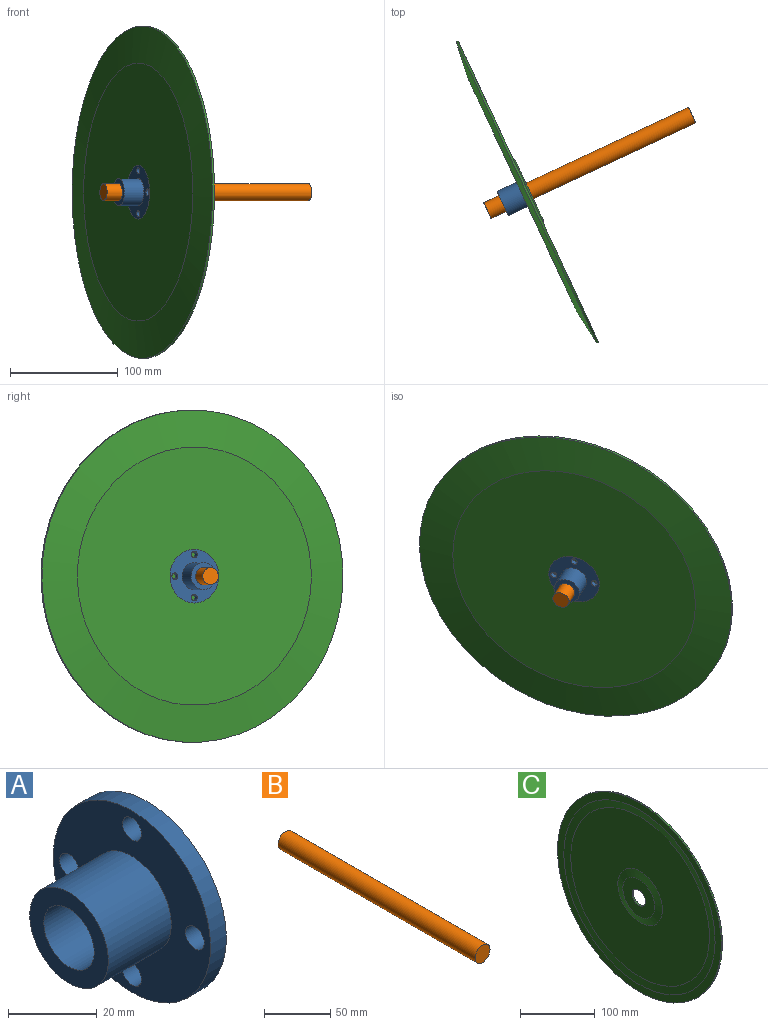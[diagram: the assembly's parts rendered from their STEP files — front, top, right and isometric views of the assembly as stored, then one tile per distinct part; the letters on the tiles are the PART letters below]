
ASSEMBLY  parts=3 mates=2
PART A: 10 faces, bbox 25x50x50 mm
  f0: plane 50x50mm, normal (1,0,0), area 1649.3mm2, adj f1,f5,f6,f7,f8,f9
  f1: cylinder r=25mm len=50mm, axis (1,0,0), area 785.4mm2, adj f0,f2
  f2: plane 50x50mm, normal (-1,0,0), area 1359.5mm2, adj f1,f3,f6,f7,f8,f9
  f3: cylinder r=12.5mm len=25mm, axis (1,0,0), area 1570.8mm2, adj f2,f4
  f4: plane 25x25mm, normal (-1,0,0), area 289.8mm2, adj f3,f5
  f5: cylinder r=8mm len=25mm, axis (-1,0,0), area 1256.6mm2, adj f0,f4
  f6: cylinder r=3mm len=6mm, axis (-1,0,0), area 94.2mm2, adj f0,f2
  f7: cylinder r=3mm len=6mm, axis (-1,0,0), area 94.2mm2, adj f0,f2
  f8: cylinder r=3mm len=6mm, axis (-1,0,0), area 94.2mm2, adj f0,f2
  f9: cylinder r=3mm len=6mm, axis (-1,0,0), area 94.2mm2, adj f0,f2
PART B: 3 faces, bbox 16x210x16 mm
  f0: cylinder r=8mm len=210mm, axis (0,1,0), area 10555.8mm2, adj f1,f2
  f1: plane 16x16mm, normal (0,-1,0), area 201.1mm2, adj f0
  f2: plane 16x16mm, normal (0,1,0), area 201.1mm2, adj f0
PART C: 11 faces, bbox 7.6x308.9x308.9 mm
  f0: cylinder r=12.5mm len=25mm, axis (-1,0,0), area 200.3mm2, adj f5,f10
  f1: plane 308.93x308.93mm, normal (-1,0,0), area 11019mm2, adj f2,f8
  f2: cone r=142.66mm half-angle=84.1deg, axis (-1,0,0), area 10297.4mm2, adj f1,f3
  f3: plane 261.46x261.46mm, normal (-1,0,0), area 48151mm2, adj f2,f4
  f4: cone r=42mm half-angle=78deg, axis (1,0,0), area 2775mm2, adj f3,f5
  f5: plane 60x60mm, normal (-1,0,0), area 2336.6mm2, adj f0,f4
  f6: plane 240x240mm, normal (1,0,0), area 43275.4mm2, adj f7,f9
  f7: cone r=120mm half-angle=83deg, axis (-1,0,0), area 29939mm2, adj f6,f8
  f8: cylinder r=154.46mm len=308.93mm, axis (-1,0,0), area 1941mm2, adj f1,f7
  f9: cylinder r=25mm len=50mm, axis (1,0,0), area 785.4mm2, adj f6,f10
  f10: plane 50x50mm, normal (1,0,0), area 1472.6mm2, adj f0,f9
PLACE A rot(axis=(0,0,1),25deg) t=(-268.9,431.41,-79.61)mm
PLACE B rot(axis=(0.64,-0.41,0.64),135.3deg) t=(-322.18,406.57,-79.61)mm
PLACE C rot(axis=(0,0,-1),155deg) t=(-289.88,421.63,-79.61)mm
MATE planar A.f1 <-> C.f9  axis (0.91,0.42,0) through (-285.35,423.74,-79.61)mm
MATE cylindrical B.f0 <-> A.f1  axis (-0.91,-0.42,0) through (-227.01,450.94,-79.61)mm
